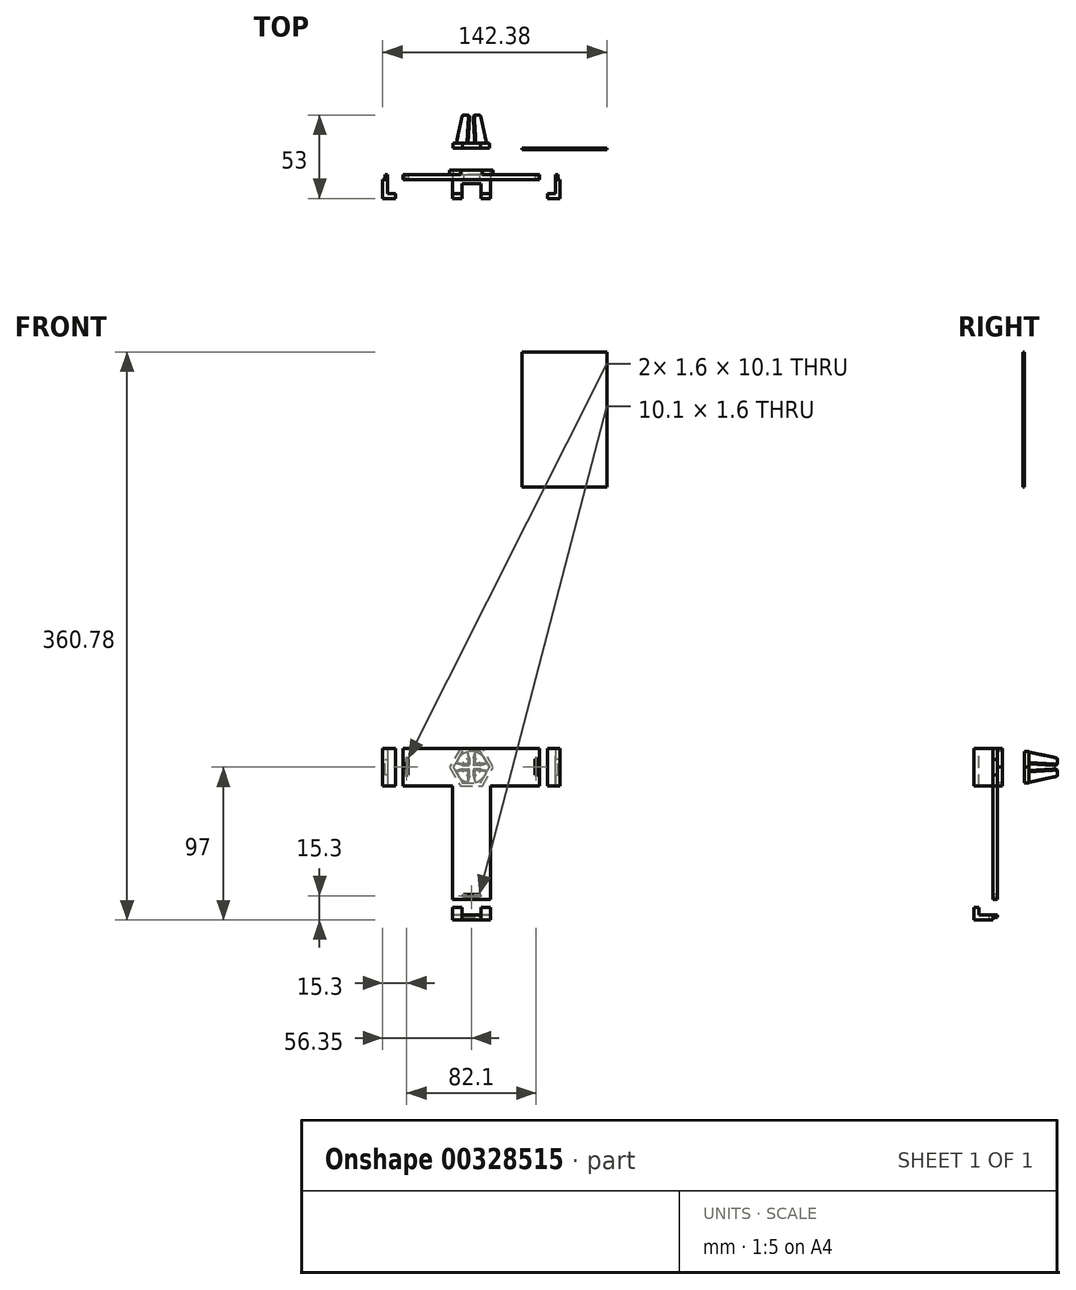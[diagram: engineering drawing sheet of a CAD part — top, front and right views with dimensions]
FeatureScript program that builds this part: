
annotation { "Feature Type Name" : "Feature", "Feature Type Description" : "" }
export const myFeature = defineFeature(function(context is Context, id is Id, definition is map)
    precondition{}
    {
        {
            assignVariable(context, id + "F0", {"name" : "depth_phone", "anyValue" : 8.5});
        }
        {
            var Q0;
            Q0=qCreatedBy(makeId("Front.planeOp"),FACE);
            var sketch = newSketch(context, id + "F1", { "sketchPlane" : qUnion([Q0])});
            skCircle(sketch, "E0", {"center": v(0, 0) * mm, "radius": 10 * mm});
            skSolve(sketch);
        }
        {
            var Q0;
            Q0=qSketchRegion(id+"F1",true);
            extrude(context, id + "F2", {"entities" : qUnion([Q0]), "oppositeDirection" : true, "depth" : 3 * mm});
        }
        {
            var Q0;
            Q0=makeQuery(id+"F2.opExtrude","CAP_FACE",FACE,{"disambiguationData":[OSD([sQuery(id+"F1.wireOp",EDGE,"E0")])],"isStart":false});
            var sketch = newSketch(context, id + "F3", { "sketchPlane" : qUnion([Q0])});
            skLineSegment(sketch, "E1.top", {"start": v(-9.75, 2.2) * mm, "end": v(-2.2, 2.2) * mm});
            skLineSegment(sketch, "E1.right", {"start": v(-2.2, 9.75) * mm, "end": v(-2.2, 2.2) * mm});
            skArc(sketch, "E2", {"start": v(-2.2, 9.75) * mm, "mid": v(-7.07, 7.07) * mm, "end": v(-9.75, 2.2) * mm});
            skLineSegment(sketch, "E3.1.0", {"start": v(-9.75, -2.2) * mm, "end": v(-2.2, -2.2) * mm});
            skLineSegment(sketch, "E3.1.1", {"start": v(-2.2, -9.75) * mm, "end": v(-2.2, -2.2) * mm});
            skArc(sketch, "E3.1.2", {"start": v(-9.75, -2.2) * mm, "mid": v(-7.07, -7.07) * mm, "end": v(-2.2, -9.75) * mm});
            skLineSegment(sketch, "E3.2.0", {"start": v(2.2, -9.75) * mm, "end": v(2.2, -2.2) * mm});
            skLineSegment(sketch, "E3.2.1", {"start": v(9.75, -2.2) * mm, "end": v(2.2, -2.2) * mm});
            skArc(sketch, "E3.2.2", {"start": v(2.2, -9.75) * mm, "mid": v(7.07, -7.07) * mm, "end": v(9.75, -2.2) * mm});
            skLineSegment(sketch, "E4.2.3.0", {"start": v(9.75, 2.2) * mm, "end": v(2.2, 2.2) * mm});
            skLineSegment(sketch, "E4.3.3.0", {"start": v(2.2, 9.75) * mm, "end": v(2.2, 2.2) * mm});
            skArc(sketch, "E4.6.3.0", {"start": v(9.75, 2.2) * mm, "mid": v(7.07, 7.07) * mm, "end": v(2.2, 9.75) * mm});
            skSolve(sketch);
        }
        {
            var Q0;
            Q0=makeQuery(id+"F3.imprint","IMPRINT",FACE,{"disambiguationData":[TD([[makeQuery(id+"F3.imprint","IMPRINT",EDGE,{"derivedFrom":sQuery(id+"F3.wireOp",EDGE,"E1.top")}),-1.0]])]});
            cPlane(context, id + "F4", {"entities" : qUnion([Q0]), "cplaneType" : CPlaneType.OFFSET, "offset" : 18 * mm, "width" : 150 * mm, "height" : 150 * mm});
        }
        {
            var Q0;
            Q0=qCreatedBy(id+"F4.planeOp",FACE);
            var sketch = newSketch(context, id + "F5", { "sketchPlane" : qUnion([Q0])});
            skLineSegment(sketch, "E5.top", {"start": v(-5.9, 1.1) * mm, "end": v(-1.1, 1.1) * mm});
            skLineSegment(sketch, "E5.right", {"start": v(-1.11, 5.9) * mm, "end": v(-1.11, 1.1) * mm});
            skArc(sketch, "E6", {"start": v(-1.11, 5.9) * mm, "mid": v(-4.24, 4.24) * mm, "end": v(-5.9, 1.1) * mm});
            skLineSegment(sketch, "E7.1.0", {"start": v(-5.9, -1.1) * mm, "end": v(-1.1, -1.1) * mm});
            skLineSegment(sketch, "E7.1.1", {"start": v(-1.1, -5.9) * mm, "end": v(-1.11, -1.1) * mm});
            skArc(sketch, "E7.1.2", {"start": v(-5.9, -1.1) * mm, "mid": v(-4.24, -4.24) * mm, "end": v(-1.1, -5.9) * mm});
            skLineSegment(sketch, "E7.2.0", {"start": v(1.1, -5.9) * mm, "end": v(1.1, -1.1) * mm});
            skLineSegment(sketch, "E7.2.1", {"start": v(5.9, -1.1) * mm, "end": v(1.1, -1.11) * mm});
            skArc(sketch, "E7.2.2", {"start": v(1.1, -5.9) * mm, "mid": v(4.24, -4.24) * mm, "end": v(5.9, -1.1) * mm});
            skLineSegment(sketch, "E7.3.0", {"start": v(5.9, 1.1) * mm, "end": v(1.1, 1.1) * mm});
            skLineSegment(sketch, "E7.3.1", {"start": v(1.1, 5.9) * mm, "end": v(1.11, 1.1) * mm});
            skArc(sketch, "E7.3.2", {"start": v(5.9, 1.11) * mm, "mid": v(4.24, 4.24) * mm, "end": v(1.1, 5.9) * mm});
            skSolve(sketch);
        }
        {
            var Q1;
            Q1=makeQuery(id+"F5.imprint","IMPRINT",FACE,{"disambiguationData":[TD([[makeQuery(id+"F5.imprint","IMPRINT",EDGE,{"derivedFrom":sQuery(id+"F5.wireOp",EDGE,"E5.top")}),1.0]])]});
            var Q2;
            Q2=makeQuery(id+"F3.imprint","IMPRINT",FACE,{"disambiguationData":[TD([[makeQuery(id+"F3.imprint","IMPRINT",EDGE,{"derivedFrom":sQuery(id+"F3.wireOp",EDGE,"E1.top")}),1.0]])]});
            loft(context, id + "F6", {"operationType" : NewBodyOperationType.ADD, "sheetProfilesArray" : [{ "sheetProfileEntities" : qUnion([Q1]) }, { "sheetProfileEntities" : qUnion([Q2]) }]});
        }
        {
            var Q1;
            Q1=makeQuery(id+"F3.imprint","IMPRINT",FACE,{"disambiguationData":[TD([[makeQuery(id+"F3.imprint","IMPRINT",EDGE,{"derivedFrom":sQuery(id+"F3.wireOp",EDGE,"E4.2.3.0")}),-1.0]])]});
            var Q2;
            Q2=makeQuery(id+"F5.imprint","IMPRINT",FACE,{"disambiguationData":[TD([[makeQuery(id+"F5.imprint","IMPRINT",EDGE,{"derivedFrom":sQuery(id+"F5.wireOp",EDGE,"E7.3.0")}),-1.0]])]});
            loft(context, id + "F7", {"operationType" : NewBodyOperationType.ADD, "sheetProfilesArray" : [{ "sheetProfileEntities" : qUnion([Q1]) }, { "sheetProfileEntities" : qUnion([Q2]) }]});
        }
        {
            var Q1;
            Q1=makeQuery(id+"F3.imprint","IMPRINT",FACE,{"disambiguationData":[TD([[makeQuery(id+"F3.imprint","IMPRINT",EDGE,{"derivedFrom":sQuery(id+"F3.wireOp",EDGE,"E3.1.0")}),-1.0]])]});
            var Q2;
            Q2=makeQuery(id+"F5.imprint","IMPRINT",FACE,{"disambiguationData":[TD([[makeQuery(id+"F5.imprint","IMPRINT",EDGE,{"derivedFrom":sQuery(id+"F5.wireOp",EDGE,"E7.1.0")}),-1.0]])]});
            loft(context, id + "F8", {"operationType" : NewBodyOperationType.ADD, "sheetProfilesArray" : [{ "sheetProfileEntities" : qUnion([Q1]) }, { "sheetProfileEntities" : qUnion([Q2]) }]});
        }
        {
            var Q1;
            Q1=makeQuery(id+"F3.imprint","IMPRINT",FACE,{"disambiguationData":[TD([[makeQuery(id+"F3.imprint","IMPRINT",EDGE,{"derivedFrom":sQuery(id+"F3.wireOp",EDGE,"E3.2.0")}),-1.0]])]});
            var Q2;
            Q2=makeQuery(id+"F5.imprint","IMPRINT",FACE,{"disambiguationData":[TD([[makeQuery(id+"F5.imprint","IMPRINT",EDGE,{"derivedFrom":sQuery(id+"F5.wireOp",EDGE,"E7.2.0")}),-1.0]])]});
            loft(context, id + "F9", {"operationType" : NewBodyOperationType.ADD, "sheetProfilesArray" : [{ "sheetProfileEntities" : qUnion([Q1]) }, { "sheetProfileEntities" : qUnion([Q2]) }]});
        }
        {
            var Q0;
            {var subQ0=sQuery(id+"F5.wireOp",EDGE,"E6");var subQ1=sQuery(id+"F5.wireOp",EDGE,"E5.right");var subQ2=sQuery(id+"F5.wireOp",EDGE,"E5.top");Q0=makeQuery(id+"F6.opLoft","MID_CAP_EDGE",EDGE,{"disambiguationData":[OSD([subQ2,subQ1,subQ0]),TDD([makeQuery(id+"F5.imprint","INTERSECT",VERTEX,{"derivedFrom":[subQ2,subQ0]}),makeQuery(id+"F5.imprint","INTERSECT",VERTEX,{"derivedFrom":[subQ1,subQ0]}),makeQuery(id+"F5.imprint","IMPRINT",EDGE,{"derivedFrom":subQ0})])],"capPos":0.0});}
            var Q1;
            Q1=makeQuery(id+"F6.opLoft","SWEPT_EDGE",EDGE,{"disambiguationData":[OSD([sQuery(id+"F3.wireOp",EDGE,"E1.right"),sQuery(id+"F3.wireOp",EDGE,"E2"),sQuery(id+"F5.wireOp",EDGE,"E5.right"),sQuery(id+"F5.wireOp",EDGE,"E6")])]});
            var Q2;
            Q2=makeQuery(id+"F6.opLoft","SWEPT_EDGE",EDGE,{"disambiguationData":[OSD([sQuery(id+"F3.wireOp",EDGE,"E1.top"),sQuery(id+"F3.wireOp",EDGE,"E1.right"),sQuery(id+"F5.wireOp",EDGE,"E5.top"),sQuery(id+"F5.wireOp",EDGE,"E5.right")])]});
            var Q3;
            Q3=makeQuery(id+"F6.opLoft","SWEPT_EDGE",EDGE,{"disambiguationData":[OSD([sQuery(id+"F3.wireOp",EDGE,"E1.top"),sQuery(id+"F3.wireOp",EDGE,"E2"),sQuery(id+"F5.wireOp",EDGE,"E5.top"),sQuery(id+"F5.wireOp",EDGE,"E6")])]});
            var Q4;
            {var subQ0=sQuery(id+"F5.wireOp",EDGE,"E7.1.2");var subQ1=sQuery(id+"F5.wireOp",EDGE,"E7.1.1");var subQ2=sQuery(id+"F5.wireOp",EDGE,"E7.1.0");Q4=makeQuery(id+"F8.opLoft","MID_CAP_EDGE",EDGE,{"disambiguationData":[OSD([subQ2,subQ1,subQ0]),TDD([makeQuery(id+"F5.imprint","INTERSECT",VERTEX,{"derivedFrom":[subQ2,subQ0]}),makeQuery(id+"F5.imprint","INTERSECT",VERTEX,{"derivedFrom":[subQ1,subQ0]}),makeQuery(id+"F5.imprint","IMPRINT",EDGE,{"derivedFrom":subQ0})])],"capPos":1.0});}
            var Q5;
            Q5=makeQuery(id+"F8.opLoft","SWEPT_EDGE",EDGE,{"disambiguationData":[OSD([sQuery(id+"F3.wireOp",EDGE,"E3.1.0"),sQuery(id+"F3.wireOp",EDGE,"E3.1.2"),sQuery(id+"F5.wireOp",EDGE,"E7.1.0"),sQuery(id+"F5.wireOp",EDGE,"E7.1.2")])]});
            var Q6;
            Q6=makeQuery(id+"F8.opLoft","SWEPT_EDGE",EDGE,{"disambiguationData":[OSD([sQuery(id+"F3.wireOp",EDGE,"E3.1.0"),sQuery(id+"F3.wireOp",EDGE,"E3.1.1"),sQuery(id+"F5.wireOp",EDGE,"E7.1.0"),sQuery(id+"F5.wireOp",EDGE,"E7.1.1")])]});
            var Q7;
            Q7=makeQuery(id+"F8.opLoft","SWEPT_EDGE",EDGE,{"disambiguationData":[OSD([sQuery(id+"F3.wireOp",EDGE,"E3.1.1"),sQuery(id+"F3.wireOp",EDGE,"E3.1.2"),sQuery(id+"F5.wireOp",EDGE,"E7.1.1"),sQuery(id+"F5.wireOp",EDGE,"E7.1.2")])]});
            var Q8;
            {var subQ0=sQuery(id+"F5.wireOp",EDGE,"E7.2.2");var subQ1=sQuery(id+"F5.wireOp",EDGE,"E7.2.1");var subQ2=sQuery(id+"F5.wireOp",EDGE,"E7.2.0");Q8=makeQuery(id+"F9.opLoft","MID_CAP_EDGE",EDGE,{"disambiguationData":[OSD([subQ2,subQ1,subQ0]),TDD([makeQuery(id+"F5.imprint","INTERSECT",VERTEX,{"derivedFrom":[subQ2,subQ0]}),makeQuery(id+"F5.imprint","INTERSECT",VERTEX,{"derivedFrom":[subQ1,subQ0]}),makeQuery(id+"F5.imprint","IMPRINT",EDGE,{"derivedFrom":subQ0})])],"capPos":1.0});}
            var Q9;
            Q9=makeQuery(id+"F9.opLoft","SWEPT_EDGE",EDGE,{"disambiguationData":[OSD([sQuery(id+"F3.wireOp",EDGE,"E3.2.0"),sQuery(id+"F3.wireOp",EDGE,"E3.2.2"),sQuery(id+"F5.wireOp",EDGE,"E7.2.0"),sQuery(id+"F5.wireOp",EDGE,"E7.2.2")])]});
            var Q10;
            Q10=makeQuery(id+"F9.opLoft","SWEPT_EDGE",EDGE,{"disambiguationData":[OSD([sQuery(id+"F3.wireOp",EDGE,"E3.2.1"),sQuery(id+"F3.wireOp",EDGE,"E3.2.2"),sQuery(id+"F5.wireOp",EDGE,"E7.2.1"),sQuery(id+"F5.wireOp",EDGE,"E7.2.2")])]});
            var Q11;
            Q11=makeQuery(id+"F9.opLoft","SWEPT_EDGE",EDGE,{"disambiguationData":[OSD([sQuery(id+"F3.wireOp",EDGE,"E3.2.0"),sQuery(id+"F3.wireOp",EDGE,"E3.2.1"),sQuery(id+"F5.wireOp",EDGE,"E7.2.0"),sQuery(id+"F5.wireOp",EDGE,"E7.2.1")])]});
            var Q12;
            {var subQ0=sQuery(id+"F5.wireOp",EDGE,"E7.3.2");var subQ1=sQuery(id+"F5.wireOp",EDGE,"E7.3.1");var subQ2=sQuery(id+"F5.wireOp",EDGE,"E7.3.0");Q12=makeQuery(id+"F7.opLoft","MID_CAP_EDGE",EDGE,{"disambiguationData":[OSD([subQ2,subQ1,subQ0]),TDD([makeQuery(id+"F5.imprint","INTERSECT",VERTEX,{"derivedFrom":[subQ2,subQ0]}),makeQuery(id+"F5.imprint","INTERSECT",VERTEX,{"derivedFrom":[subQ1,subQ0]}),makeQuery(id+"F5.imprint","IMPRINT",EDGE,{"derivedFrom":subQ0})])],"capPos":1.0});}
            var Q13;
            Q13=makeQuery(id+"F7.opLoft","SWEPT_EDGE",EDGE,{"disambiguationData":[OSD([sQuery(id+"F3.wireOp",EDGE,"E4.2.3.0"),sQuery(id+"F3.wireOp",EDGE,"E4.3.3.0"),sQuery(id+"F5.wireOp",EDGE,"E7.3.0"),sQuery(id+"F5.wireOp",EDGE,"E7.3.1")])]});
            var Q14;
            Q14=makeQuery(id+"F7.opLoft","SWEPT_EDGE",EDGE,{"disambiguationData":[OSD([sQuery(id+"F3.wireOp",EDGE,"E4.2.3.0"),sQuery(id+"F3.wireOp",EDGE,"E4.6.3.0"),sQuery(id+"F5.wireOp",EDGE,"E7.3.0"),sQuery(id+"F5.wireOp",EDGE,"E7.3.2")])]});
            var Q15;
            Q15=makeQuery(id+"F7.opLoft","SWEPT_EDGE",EDGE,{"disambiguationData":[OSD([sQuery(id+"F3.wireOp",EDGE,"E4.3.3.0"),sQuery(id+"F3.wireOp",EDGE,"E4.6.3.0"),sQuery(id+"F5.wireOp",EDGE,"E7.3.1"),sQuery(id+"F5.wireOp",EDGE,"E7.3.2")])]});
            fillet(context, id + "F10", {"entities" : qUnion([Q0, Q1, Q2, Q3, Q4, Q5, Q6, Q7, Q8, Q9, Q10, Q11, Q12, Q13, Q14, Q15]), "radius" : .5 * mm, "tangentPropagation" : true, "allowEdgeOverflow" : false});
        }
        {
            var Q0;
            Q0=qCreatedBy(makeId("Front.planeOp"),FACE);
            var sketch = newSketch(context, id + "F11", { "sketchPlane" : qUnion([Q0])});
            skLineSegment(sketch, "E8.bottom", {"start": v(86.03, 177.78) * mm, "end": v(32.03, 177.78) * mm});
            skLineSegment(sketch, "E8.top", {"start": v(86.03, 263.78) * mm, "end": v(32.03, 263.78) * mm});
            skLineSegment(sketch, "E8.left", {"start": v(86.03, 177.78) * mm, "end": v(86.03, 263.78) * mm});
            skLineSegment(sketch, "E8.right", {"start": v(32.03, 177.78) * mm, "end": v(32.03, 263.78) * mm});
            skSolve(sketch);
        }
        {
            var Q0;
            Q0=makeQuery(id+"F11.imprint","IMPRINT",FACE,{"disambiguationData":[TD([[makeQuery(id+"F11.imprint","IMPRINT",EDGE,{"derivedFrom":sQuery(id+"F11.wireOp",EDGE,"E8.bottom")}),-1.0]])]});
            extrude(context, id + "F12", {"entities" : qUnion([Q0]), "depth" : 1 * mm});
        }
        {
            var Q0;
            {var subQ0=sQuery(id+"F5.wireOp",EDGE,"E5.right");var subQ1=sQuery(id+"F5.wireOp",EDGE,"E6");var subQ2=sQuery(id+"F5.wireOp",EDGE,"E5.top");Q0=makeQuery(id+"F6.opLoft","MID_CAP_EDGE",EDGE,{"disambiguationData":[OSD([subQ2,subQ0,subQ1]),TDD([makeQuery(id+"F5.imprint","INTERSECT",VERTEX,{"derivedFrom":[subQ2,subQ0]}),makeQuery(id+"F5.imprint","INTERSECT",VERTEX,{"derivedFrom":[subQ0,subQ1]}),makeQuery(id+"F5.imprint","IMPRINT",EDGE,{"derivedFrom":subQ0})])],"capPos":0.0});}
            var Q1;
            {var subQ0=sQuery(id+"F5.wireOp",EDGE,"E5.top");var subQ1=sQuery(id+"F5.wireOp",EDGE,"E5.right");var subQ2=sQuery(id+"F5.wireOp",EDGE,"E6");Q1=makeQuery(id+"F6.opLoft","MID_CAP_EDGE",EDGE,{"disambiguationData":[OSD([subQ0,subQ1,subQ2]),TDD([makeQuery(id+"F5.imprint","INTERSECT",VERTEX,{"derivedFrom":[subQ0,subQ2]}),makeQuery(id+"F5.imprint","INTERSECT",VERTEX,{"derivedFrom":[subQ0,subQ1]}),makeQuery(id+"F5.imprint","IMPRINT",EDGE,{"derivedFrom":subQ0})])],"capPos":0.0});}
            var Q2;
            {var subQ0=sQuery(id+"F5.wireOp",EDGE,"E7.1.0");var subQ1=sQuery(id+"F5.wireOp",EDGE,"E7.1.1");var subQ2=sQuery(id+"F5.wireOp",EDGE,"E7.1.2");Q2=makeQuery(id+"F8.opLoft","MID_CAP_EDGE",EDGE,{"disambiguationData":[OSD([subQ0,subQ1,subQ2]),TDD([makeQuery(id+"F5.imprint","INTERSECT",VERTEX,{"derivedFrom":[subQ0,subQ2]}),makeQuery(id+"F5.imprint","INTERSECT",VERTEX,{"derivedFrom":[subQ0,subQ1]}),makeQuery(id+"F5.imprint","IMPRINT",EDGE,{"derivedFrom":subQ0})])],"capPos":1.0});}
            var Q3;
            {var subQ0=sQuery(id+"F5.wireOp",EDGE,"E7.1.1");var subQ1=sQuery(id+"F5.wireOp",EDGE,"E7.1.2");var subQ2=sQuery(id+"F5.wireOp",EDGE,"E7.1.0");Q3=makeQuery(id+"F8.opLoft","MID_CAP_EDGE",EDGE,{"disambiguationData":[OSD([subQ2,subQ0,subQ1]),TDD([makeQuery(id+"F5.imprint","INTERSECT",VERTEX,{"derivedFrom":[subQ2,subQ0]}),makeQuery(id+"F5.imprint","INTERSECT",VERTEX,{"derivedFrom":[subQ0,subQ1]}),makeQuery(id+"F5.imprint","IMPRINT",EDGE,{"derivedFrom":subQ0})])],"capPos":1.0});}
            var Q4;
            {var subQ0=sQuery(id+"F5.wireOp",EDGE,"E7.2.0");var subQ1=sQuery(id+"F5.wireOp",EDGE,"E7.2.1");var subQ2=sQuery(id+"F5.wireOp",EDGE,"E7.2.2");Q4=makeQuery(id+"F9.opLoft","MID_CAP_EDGE",EDGE,{"disambiguationData":[OSD([subQ0,subQ1,subQ2]),TDD([makeQuery(id+"F5.imprint","INTERSECT",VERTEX,{"derivedFrom":[subQ0,subQ2]}),makeQuery(id+"F5.imprint","INTERSECT",VERTEX,{"derivedFrom":[subQ0,subQ1]}),makeQuery(id+"F5.imprint","IMPRINT",EDGE,{"derivedFrom":subQ0})])],"capPos":1.0});}
            var Q5;
            {var subQ0=sQuery(id+"F5.wireOp",EDGE,"E7.2.1");var subQ1=sQuery(id+"F5.wireOp",EDGE,"E7.2.2");var subQ2=sQuery(id+"F5.wireOp",EDGE,"E7.2.0");Q5=makeQuery(id+"F9.opLoft","MID_CAP_EDGE",EDGE,{"disambiguationData":[OSD([subQ2,subQ0,subQ1]),TDD([makeQuery(id+"F5.imprint","INTERSECT",VERTEX,{"derivedFrom":[subQ2,subQ0]}),makeQuery(id+"F5.imprint","INTERSECT",VERTEX,{"derivedFrom":[subQ0,subQ1]}),makeQuery(id+"F5.imprint","IMPRINT",EDGE,{"derivedFrom":subQ0})])],"capPos":1.0});}
            var Q6;
            {var subQ0=sQuery(id+"F5.wireOp",EDGE,"E7.3.0");var subQ1=sQuery(id+"F5.wireOp",EDGE,"E7.3.1");var subQ2=sQuery(id+"F5.wireOp",EDGE,"E7.3.2");Q6=makeQuery(id+"F7.opLoft","MID_CAP_EDGE",EDGE,{"disambiguationData":[OSD([subQ0,subQ1,subQ2]),TDD([makeQuery(id+"F5.imprint","INTERSECT",VERTEX,{"derivedFrom":[subQ0,subQ2]}),makeQuery(id+"F5.imprint","INTERSECT",VERTEX,{"derivedFrom":[subQ0,subQ1]}),makeQuery(id+"F5.imprint","IMPRINT",EDGE,{"derivedFrom":subQ0})])],"capPos":1.0});}
            var Q7;
            {var subQ0=sQuery(id+"F5.wireOp",EDGE,"E7.3.1");var subQ1=sQuery(id+"F5.wireOp",EDGE,"E7.3.2");var subQ2=sQuery(id+"F5.wireOp",EDGE,"E7.3.0");Q7=makeQuery(id+"F7.opLoft","MID_CAP_EDGE",EDGE,{"disambiguationData":[OSD([subQ2,subQ0,subQ1]),TDD([makeQuery(id+"F5.imprint","INTERSECT",VERTEX,{"derivedFrom":[subQ2,subQ0]}),makeQuery(id+"F5.imprint","INTERSECT",VERTEX,{"derivedFrom":[subQ0,subQ1]}),makeQuery(id+"F5.imprint","IMPRINT",EDGE,{"derivedFrom":subQ0})])],"capPos":1.0});}
            fillet(context, id + "F13", {"entities" : qUnion([Q0, Q1, Q2, Q3, Q4, Q5, Q6, Q7]), "radius" : 1.5 * mm, "tangentPropagation" : true, "allowEdgeOverflow" : false});
        }
        {
            var Q0;
            Q0=qCreatedBy(makeId("Front.planeOp"),FACE);
            var sketch = newSketch(context, id + "F14", { "sketchPlane" : qUnion([Q0])});
            skLineSegment(sketch, "E9.bottom", {"start": v(102.82, 54.15) * mm, "end": v(182.82, 54.15) * mm});
            skLineSegment(sketch, "E9.top", {"start": v(102.82, -107.85) * mm, "end": v(182.82, -107.85) * mm});
            skLineSegment(sketch, "E9.left", {"start": v(102.82, 54.15) * mm, "end": v(102.82, -107.85) * mm});
            skLineSegment(sketch, "E9.right", {"start": v(182.82, 54.15) * mm, "end": v(182.82, -107.85) * mm});
            skSolve(sketch);
        }
        {
            var Q0;
            Q0=qSketchRegion(id+"F14",true);
            extrude(context, id + "F15", {"entities" : qUnion([Q0]), "depth" : (getVariable(context, 'depth_phone')) * mm});
        }
        {
            var Q0;
            Q0=makeQuery(id+"F15.opExtrude","SWEPT_EDGE",EDGE,{"disambiguationData":[OSD([sQuery(id+"F14.wireOp",EDGE,"E9.bottom"),sQuery(id+"F14.wireOp",EDGE,"E9.left")])]});
            var Q1;
            Q1=makeQuery(id+"F15.opExtrude","SWEPT_EDGE",EDGE,{"disambiguationData":[OSD([sQuery(id+"F14.wireOp",EDGE,"E9.bottom"),sQuery(id+"F14.wireOp",EDGE,"E9.right")])]});
            var Q2;
            Q2=makeQuery(id+"F15.opExtrude","SWEPT_EDGE",EDGE,{"disambiguationData":[OSD([sQuery(id+"F14.wireOp",EDGE,"E9.top"),sQuery(id+"F14.wireOp",EDGE,"E9.right")])]});
            var Q3;
            Q3=makeQuery(id+"F15.opExtrude","SWEPT_EDGE",EDGE,{"disambiguationData":[OSD([sQuery(id+"F14.wireOp",EDGE,"E9.top"),sQuery(id+"F14.wireOp",EDGE,"E9.left")])]});
            fillet(context, id + "F16", {"entities" : qUnion([Q0, Q1, Q2, Q3]), "radius" : 2.5 * mm, "tangentPropagation" : true, "allowEdgeOverflow" : false});
        }
        {
            var Q0;
            Q0=makeQuery(id+"F15.opExtrude","CAP_EDGE",EDGE,{"disambiguationData":[OSD([sQuery(id+"F14.wireOp",EDGE,"E9.right")])],"isStart":true});
            var Q1;
            Q1=makeQuery(id+"F15.opExtrude","CAP_EDGE",EDGE,{"disambiguationData":[OSD([sQuery(id+"F14.wireOp",EDGE,"E9.bottom")])],"isStart":true});
            var Q2;
            Q2=makeQuery(id+"F15.opExtrude","CAP_EDGE",EDGE,{"disambiguationData":[OSD([sQuery(id+"F14.wireOp",EDGE,"E9.left")])],"isStart":true});
            var Q3;
            Q3=makeQuery(id+"F15.opExtrude","CAP_EDGE",EDGE,{"disambiguationData":[OSD([sQuery(id+"F14.wireOp",EDGE,"E9.top")])],"isStart":true});
            fillet(context, id + "F17", {"entities" : qUnion([Q0, Q1, Q2, Q3]), "radius" : 2.5 * mm, "tangentPropagation" : true, "allowEdgeOverflow" : false});
        }
        {
            var Q0;
            Q0=makeQuery(id+"F15.opExtrude","CAP_EDGE",EDGE,{"disambiguationData":[OSD([sQuery(id+"F14.wireOp",EDGE,"E9.right")])],"isStart":false});
            var Q1;
            Q1=makeQuery(id+"F15.opExtrude","CAP_EDGE",EDGE,{"disambiguationData":[OSD([sQuery(id+"F14.wireOp",EDGE,"E9.bottom")])],"isStart":false});
            var Q2;
            Q2=makeQuery(id+"F15.opExtrude","CAP_EDGE",EDGE,{"disambiguationData":[OSD([sQuery(id+"F14.wireOp",EDGE,"E9.left")])],"isStart":false});
            var Q3;
            Q3=makeQuery(id+"F15.opExtrude","CAP_EDGE",EDGE,{"disambiguationData":[OSD([sQuery(id+"F14.wireOp",EDGE,"E9.top")])],"isStart":false});
            fillet(context, id + "F18", {"entities" : qUnion([Q0, Q1, Q2, Q3]), "radius" : 12 * mm, "tangentPropagation" : true, "allowEdgeOverflow" : false});
        }
        {
            var Q0;
            Q0=qCreatedBy(makeId("Front.planeOp"),FACE);
            cPlane(context, id + "F19", {"entities" : qUnion([Q0]), "cplaneType" : CPlaneType.OFFSET, "offset" : 20 * mm, "width" : 150 * mm, "height" : 150 * mm});
        }
        {
            var Q0;
            Q0=qCreatedBy(id+"F19.planeOp",FACE);
            var sketch = newSketch(context, id + "F20", { "sketchPlane" : qUnion([Q0])});
            skLineSegment(sketch, "E10.bottom", {"start": v(-12, -84) * mm, "end": v(12, -84) * mm});
            skLineSegment(sketch, "E10.top", {"start": v(-12, 0) * mm, "end": v(12, 0) * mm});
            skLineSegment(sketch, "E10.left", {"start": v(-12, -84) * mm, "end": v(-12, 0) * mm});
            skLineSegment(sketch, "E10.right", {"start": v(12, -84) * mm, "end": v(12, 0) * mm});
            skSolve(sketch);
        }
        {
            var Q0;
            Q0=qSketchRegion(id+"F20",true);
            extrude(context, id + "F21", {"entities" : qUnion([Q0]), "operationType" : NewBodyOperationType.ADD, "oppositeDirection" : true, "depth" : 3 * mm});
        }
        {
            var Q0;
            Q0=makeQuery(id+"F21.opExtrude","SWEPT_FACE",FACE,{"disambiguationData":[OSD([sQuery(id+"F20.wireOp",EDGE,"E10.bottom")])]});
            cPlane(context, id + "F22", {"entities" : qUnion([Q0]), "cplaneType" : CPlaneType.OFFSET, "offset" : 10 * mm, "width" : 150 * mm, "height" : 150 * mm});
        }
        {
            var Q0;
            Q0=qCreatedBy(id+"F22.planeOp",FACE);
            var sketch = newSketch(context, id + "F23", { "sketchPlane" : qUnion([Q0])});
            skLineSegment(sketch, "E11.bottom", {"start": v(12, 17) * mm, "end": v(-12, 17) * mm});
            skLineSegment(sketch, "E11.top", {"start": v(12, 29) * mm, "end": v(-12, 29) * mm});
            skLineSegment(sketch, "E11.left", {"start": v(12, 17) * mm, "end": v(12, 29) * mm});
            skLineSegment(sketch, "E11.right", {"start": v(-12, 17) * mm, "end": v(-12, 29) * mm});
            skSolve(sketch);
        }
        {
            var Q0;
            Q0=qSketchRegion(id+"F23",true);
            extrude(context, id + "F24", {"entities" : qUnion([Q0]), "operationType" : NewBodyOperationType.ADD, "depth" : 3 * mm});
        }
        {
            var Q0;
            Q0=qCreatedBy(id+"F19.planeOp",FACE);
            var sketch = newSketch(context, id + "F25", { "sketchPlane" : qUnion([Q0])});
            skLineSegment(sketch, "E12.bottom", {"start": v(43.35, 12) * mm, "end": v(-43.35, 12) * mm});
            skLineSegment(sketch, "E12.top", {"start": v(43.35, -12) * mm, "end": v(-43.35, -12) * mm});
            skLineSegment(sketch, "E12.left", {"start": v(43.35, 12) * mm, "end": v(43.35, -12) * mm});
            skLineSegment(sketch, "E12.right", {"start": v(-43.35, 12) * mm, "end": v(-43.35, -12) * mm});
            skLineSegment(sketch, "E13", {"start": v(43.35, 0) * mm, "end": v(-43.35, 0) * mm, "construction": true});
            skLineSegment(sketch, "E14", {"start": v(0, -12) * mm, "end": v(0, 12) * mm, "construction": true});
            skPoint(sketch, "E15", {"position": v(0, 0) * mm});
            skSolve(sketch);
        }
        {
            var Q0;
            Q0=makeQuery(id+"F25.imprint","IMPRINT",FACE,{"disambiguationData":[TD([[makeQuery(id+"F25.imprint","IMPRINT",EDGE,{"derivedFrom":sQuery(id+"F25.wireOp",EDGE,"E12.bottom")}),1.0]])]});
            extrude(context, id + "F26", {"entities" : qUnion([Q0]), "operationType" : NewBodyOperationType.ADD, "oppositeDirection" : true, "depth" : 3 * mm});
        }
        {
            var Q0;
            Q0=makeQuery(id+"F26.opExtrude","SWEPT_FACE",FACE,{"disambiguationData":[OSD([sQuery(id+"F25.wireOp",EDGE,"E12.right")])]});
            cPlane(context, id + "F27", {"entities" : qUnion([Q0]), "cplaneType" : CPlaneType.OFFSET, "offset" : 10 * mm, "width" : 150 * mm, "height" : 150 * mm});
        }
        {
            var Q0;
            Q0=qCreatedBy(id+"F27.planeOp",FACE);
            var sketch = newSketch(context, id + "F28", { "sketchPlane" : qUnion([Q0])});
            skLineSegment(sketch, "E16.bottom", {"start": v(17, 12) * mm, "end": v(29, 12) * mm});
            skLineSegment(sketch, "E16.top", {"start": v(17, -12) * mm, "end": v(29, -12) * mm});
            skLineSegment(sketch, "E16.left", {"start": v(17, 12) * mm, "end": v(17, -12) * mm});
            skLineSegment(sketch, "E16.right", {"start": v(29, 12) * mm, "end": v(29, -12) * mm});
            skSolve(sketch);
        }
        {
            var Q0;
            Q0=qSketchRegion(id+"F28",true);
            extrude(context, id + "F29", {"entities" : qUnion([Q0]), "operationType" : NewBodyOperationType.ADD, "depth" : 3 * mm});
        }
        {
            var Q0;
            Q0=makeQuery(id+"F26.opExtrude","SWEPT_FACE",FACE,{"disambiguationData":[OSD([sQuery(id+"F25.wireOp",EDGE,"E12.left")])]});
            cPlane(context, id + "F30", {"entities" : qUnion([Q0]), "cplaneType" : CPlaneType.OFFSET, "offset" : 10 * mm, "width" : 150 * mm, "height" : 150 * mm});
        }
        {
            var Q0;
            Q0=qCreatedBy(id+"F30.planeOp",FACE);
            var sketch = newSketch(context, id + "F31", { "sketchPlane" : qUnion([Q0])});
            skLineSegment(sketch, "E17.bottom", {"start": v(-17, -12) * mm, "end": v(-29, -12) * mm});
            skLineSegment(sketch, "E17.top", {"start": v(-17, 12) * mm, "end": v(-29, 12) * mm});
            skLineSegment(sketch, "E17.left", {"start": v(-17, -12) * mm, "end": v(-17, 12) * mm});
            skLineSegment(sketch, "E17.right", {"start": v(-29, -12) * mm, "end": v(-29, 12) * mm});
            skSolve(sketch);
        }
        {
            var Q0;
            Q0=qSketchRegion(id+"F31",true);
            extrude(context, id + "F32", {"entities" : qUnion([Q0]), "operationType" : NewBodyOperationType.ADD, "depth" : 3 * mm});
        }
        {
            var Q0;
            Q0=makeQuery(id+"F24.opExtrude","CAP_FACE",FACE,{"disambiguationData":[OSD([sQuery(id+"F23.wireOp",EDGE,"E11.bottom"),sQuery(id+"F23.wireOp",EDGE,"E11.top"),sQuery(id+"F23.wireOp",EDGE,"E11.left"),sQuery(id+"F23.wireOp",EDGE,"E11.right")])],"isStart":false});
            var sketch = newSketch(context, id + "F33", { "sketchPlane" : qUnion([Q0])});
            skLineSegment(sketch, "E18.bottom", {"start": v(-6, 29) * mm, "end": v(6, 29) * mm});
            skLineSegment(sketch, "E18.top", {"start": v(-6, 20) * mm, "end": v(6, 20) * mm});
            skLineSegment(sketch, "E18.left", {"start": v(-6, 29) * mm, "end": v(-6, 20) * mm});
            skLineSegment(sketch, "E18.right", {"start": v(6, 29) * mm, "end": v(6, 20) * mm});
            skLineSegment(sketch, "E19", {"start": v(0, 20) * mm, "end": v(0, 29) * mm, "construction": true});
            skSolve(sketch);
        }
        {
            var Q0;
            Q0=qSketchRegion(id+"F33",true);
            extrude(context, id + "F34", {"entities" : qUnion([Q0]), "operationType" : NewBodyOperationType.REMOVE, "endBound" : BoundingType.UP_TO_NEXT, "oppositeDirection" : true, "depth" : 25 * mm});
        }
        {
            var Q0;
            Q0=makeQuery(id+"F29.opExtrude","SWEPT_FACE",FACE,{"disambiguationData":[OSD([sQuery(id+"F28.wireOp",EDGE,"E16.right")])]});
            var sketch = newSketch(context, id + "F35", { "sketchPlane" : qUnion([Q0])});
            skLineSegment(sketch, "E20.bottom", {"start": v(-56.35, -12) * mm, "end": v(-48.35, -12) * mm});
            skLineSegment(sketch, "E20.top", {"start": v(-56.35, 12) * mm, "end": v(-48.35, 12) * mm});
            skLineSegment(sketch, "E20.left", {"start": v(-56.35, -12) * mm, "end": v(-56.35, 12) * mm});
            skLineSegment(sketch, "E20.right", {"start": v(-48.35, -12) * mm, "end": v(-48.35, 12) * mm});
            skLineSegment(sketch, "E21.bottom", {"start": v(56.35, -12) * mm, "end": v(48.35, -12) * mm});
            skLineSegment(sketch, "E21.top", {"start": v(56.35, 12) * mm, "end": v(48.35, 12) * mm});
            skLineSegment(sketch, "E21.left", {"start": v(56.35, -12) * mm, "end": v(56.35, 12) * mm});
            skLineSegment(sketch, "E21.right", {"start": v(48.35, -12) * mm, "end": v(48.35, 12) * mm});
            skLineSegment(sketch, "E22.bottom", {"start": v(-12, -97) * mm, "end": v(-6, -97) * mm});
            skLineSegment(sketch, "E22.top", {"start": v(-12, -89) * mm, "end": v(-6, -89) * mm});
            skLineSegment(sketch, "E22.left", {"start": v(-12, -97) * mm, "end": v(-12, -89) * mm});
            skLineSegment(sketch, "E22.right", {"start": v(-6, -97) * mm, "end": v(-6, -89) * mm});
            skLineSegment(sketch, "E23.bottom", {"start": v(6, -97) * mm, "end": v(12, -97) * mm});
            skLineSegment(sketch, "E23.top", {"start": v(6, -89) * mm, "end": v(12, -89) * mm});
            skLineSegment(sketch, "E23.left", {"start": v(6, -97) * mm, "end": v(6, -89) * mm});
            skLineSegment(sketch, "E23.right", {"start": v(12, -97) * mm, "end": v(12, -89) * mm});
            skSolve(sketch);
        }
        {
            var Q0;
            Q0=qSketchRegion(id+"F35",true);
            extrude(context, id + "F36", {"entities" : qUnion([Q0]), "operationType" : NewBodyOperationType.ADD, "depth" : 3 * mm});
        }
        {
            var Q0;
            Q0=makeQuery(id+"F32.boolean.opBoolean","MERGE",FACE,{"derivedFrom":[makeQuery(id+"F29.boolean.opBoolean","MERGE",FACE,{"derivedFrom":[makeQuery(id+"F26.boolean.opBoolean","MERGE",FACE,{"derivedFrom":[makeQuery(id+"F24.boolean.opBoolean","MERGE",FACE,{"derivedFrom":[makeQuery(id+"F21.opExtrude","CAP_FACE",FACE,{"disambiguationData":[OSD([sQuery(id+"F20.wireOp",EDGE,"E10.bottom"),sQuery(id+"F20.wireOp",EDGE,"E10.top"),sQuery(id+"F20.wireOp",EDGE,"E10.left"),sQuery(id+"F20.wireOp",EDGE,"E10.right")])],"isStart":false}),makeQuery(id+"F24.opExtrude","SWEPT_FACE",FACE,{"disambiguationData":[OSD([sQuery(id+"F23.wireOp",EDGE,"E11.bottom")])]})]}),makeQuery(id+"F26.opExtrude","CAP_FACE",FACE,{"disambiguationData":[OSD([sQuery(id+"F25.wireOp",EDGE,"E12.bottom"),sQuery(id+"F25.wireOp",EDGE,"E12.top"),sQuery(id+"F25.wireOp",EDGE,"E12.left"),sQuery(id+"F25.wireOp",EDGE,"E12.right")])],"isStart":false})]}),makeQuery(id+"F29.opExtrude","SWEPT_FACE",FACE,{"disambiguationData":[OSD([sQuery(id+"F28.wireOp",EDGE,"E16.left")])]})]}),makeQuery(id+"F32.opExtrude","SWEPT_FACE",FACE,{"disambiguationData":[OSD([sQuery(id+"F31.wireOp",EDGE,"E17.left")])]})]});
            var sketch = newSketch(context, id + "F37", { "sketchPlane" : qUnion([Q0])});
            skCircle(sketch, "E24.cCircle", {"center": v(0, 0) * mm, "radius": 10.1 * mm, "construction": true});
            skLineSegment(sketch, "E24.0", {"start": v(11.66, 0) * mm, "end": v(5.83, -10.1) * mm});
            skLineSegment(sketch, "E24.1", {"start": v(5.83, -10.1) * mm, "end": v(-5.83, -10.1) * mm});
            skLineSegment(sketch, "E24.2", {"start": v(-5.83, -10.1) * mm, "end": v(-11.66, 0) * mm});
            skLineSegment(sketch, "E24.3", {"start": v(-11.66, 0) * mm, "end": v(-5.83, 10.1) * mm});
            skLineSegment(sketch, "E24.4", {"start": v(-5.83, 10.1) * mm, "end": v(5.83, 10.1) * mm});
            skLineSegment(sketch, "E24.5", {"start": v(5.83, 10.1) * mm, "end": v(11.66, 0) * mm});
            skPoint(sketch, "E24.0.midPoint", {"position": v(8.75, -5.05) * mm});
            skCircle(sketch, "E25.cCircle", {"center": v(0, 0) * mm, "radius": 12 * mm, "construction": true});
            skLineSegment(sketch, "E25.0", {"start": v(13.86, 0) * mm, "end": v(6.93, -12) * mm});
            skLineSegment(sketch, "E25.1", {"start": v(6.93, -12) * mm, "end": v(-6.93, -12) * mm});
            skLineSegment(sketch, "E25.2", {"start": v(-6.93, -12) * mm, "end": v(-13.86, 0) * mm});
            skLineSegment(sketch, "E25.3", {"start": v(-13.86, 0) * mm, "end": v(-6.93, 12) * mm});
            skLineSegment(sketch, "E25.4", {"start": v(-6.93, 12) * mm, "end": v(6.93, 12) * mm});
            skLineSegment(sketch, "E25.5", {"start": v(6.93, 12) * mm, "end": v(13.86, 0) * mm});
            skPoint(sketch, "E25.0.midPoint", {"position": v(10.4, -6) * mm});
            skSolve(sketch);
        }
        {
            var Q0;
            Q0=qSketchRegion(id+"F37",true);
            extrude(context, id + "F38", {"entities" : qUnion([Q0]), "operationType" : NewBodyOperationType.ADD, "depth" : 3 * mm});
        }
        {
            var Q0;
            Q0=makeQuery(id+"F2.opExtrude","CAP_FACE",FACE,{"disambiguationData":[OSD([sQuery(id+"F1.wireOp",EDGE,"E0")])],"isStart":false});
            var sketch = newSketch(context, id + "F39", { "sketchPlane" : qUnion([Q0])});
            skCircle(sketch, "E26.cCircle", {"center": v(0, 0) * mm, "radius": 10 * mm, "construction": true});
            skLineSegment(sketch, "E26.0", {"start": v(11.55, 0) * mm, "end": v(5.77, -10) * mm});
            skLineSegment(sketch, "E26.1", {"start": v(5.77, -10) * mm, "end": v(-5.77, -10) * mm});
            skLineSegment(sketch, "E26.2", {"start": v(-5.77, -10) * mm, "end": v(-11.55, 0) * mm});
            skLineSegment(sketch, "E26.3", {"start": v(-11.55, 0) * mm, "end": v(-5.77, 10) * mm});
            skLineSegment(sketch, "E26.4", {"start": v(-5.77, 10) * mm, "end": v(5.77, 10) * mm});
            skLineSegment(sketch, "E26.5", {"start": v(5.77, 10) * mm, "end": v(11.55, 0) * mm});
            skPoint(sketch, "E26.0.midPoint", {"position": v(8.66, -5) * mm});
            skSolve(sketch);
        }
        {
            var Q0;
            Q0=qSketchRegion(id+"F39",true);
            extrude(context, id + "F40", {"entities" : qUnion([Q0]), "operationType" : NewBodyOperationType.ADD, "oppositeDirection" : true, "depth" : 3 * mm});
        }
        {
            var Q0;
            Q0=makeQuery(id+"F26.boolean.opBoolean","MERGE",FACE,{"derivedFrom":[makeQuery(id+"F21.opExtrude","CAP_FACE",FACE,{"disambiguationData":[OSD([sQuery(id+"F20.wireOp",EDGE,"E10.bottom"),sQuery(id+"F20.wireOp",EDGE,"E10.top"),sQuery(id+"F20.wireOp",EDGE,"E10.left"),sQuery(id+"F20.wireOp",EDGE,"E10.right")])],"isStart":true}),makeQuery(id+"F26.opExtrude","CAP_FACE",FACE,{"disambiguationData":[OSD([sQuery(id+"F25.wireOp",EDGE,"E12.bottom"),sQuery(id+"F25.wireOp",EDGE,"E12.top"),sQuery(id+"F25.wireOp",EDGE,"E12.left"),sQuery(id+"F25.wireOp",EDGE,"E12.right")])],"isStart":true})]});
            var sketch = newSketch(context, id + "F41", { "sketchPlane" : qUnion([Q0])});
            skLineSegment(sketch, "E27.bottom", {"start": v(-41.85, 5.05) * mm, "end": v(-40.25, 5.05) * mm});
            skLineSegment(sketch, "E27.top", {"start": v(-41.85, -5.05) * mm, "end": v(-40.25, -5.05) * mm});
            skLineSegment(sketch, "E27.left", {"start": v(-41.85, 5.05) * mm, "end": v(-41.85, -5.05) * mm});
            skLineSegment(sketch, "E27.right", {"start": v(-40.25, 5.05) * mm, "end": v(-40.25, -5.05) * mm});
            skLineSegment(sketch, "E28", {"start": v(-41.85, 0) * mm, "end": v(-40.25, 0) * mm, "construction": true});
            skLineSegment(sketch, "E29", {"start": v(0, 8.73) * mm, "end": v(0, 0) * mm, "construction": true});
            skLineSegment(sketch, "E30.MirrorCS", {"start": v(40.25, 5.05) * mm, "end": v(40.25, -5.05) * mm});
            skLineSegment(sketch, "E31.MirrorCS", {"start": v(41.85, -5.05) * mm, "end": v(40.25, -5.05) * mm});
            skLineSegment(sketch, "E32.MirrorCS", {"start": v(41.85, 5.05) * mm, "end": v(41.85, -5.05) * mm});
            skLineSegment(sketch, "E33.MirrorCS", {"start": v(41.85, 5.05) * mm, "end": v(40.25, 5.05) * mm});
            skLineSegment(sketch, "E34.bottom", {"start": v(-5.05, -82.5) * mm, "end": v(5.05, -82.5) * mm});
            skLineSegment(sketch, "E34.top", {"start": v(-5.05, -80.9) * mm, "end": v(5.05, -80.9) * mm});
            skLineSegment(sketch, "E34.left", {"start": v(-5.05, -82.5) * mm, "end": v(-5.05, -80.9) * mm});
            skLineSegment(sketch, "E34.right", {"start": v(5.05, -82.5) * mm, "end": v(5.05, -80.9) * mm});
            skLineSegment(sketch, "E35", {"start": v(0, -80.9) * mm, "end": v(0, -82.5) * mm, "construction": true});
            skSolve(sketch);
        }
        {
            var Q0;
            Q0=qSketchRegion(id+"F41",true);
            extrude(context, id + "F42", {"entities" : qUnion([Q0]), "operationType" : NewBodyOperationType.REMOVE, "endBound" : BoundingType.UP_TO_NEXT, "oppositeDirection" : true, "depth" : 25 * mm});
        }
        {
            var Q0;
            Q0=qCreatedBy(id+"F19.planeOp",FACE);
            var sketch = newSketch(context, id + "F43", { "sketchPlane" : qUnion([Q0])});
            skLineSegment(sketch, "E36", {"start": v(56.35, -12) * mm, "end": v(56.35, 12) * mm});
            skLineSegment(sketch, "E37", {"start": v(56.35, 12) * mm, "end": v(53.35, 12) * mm});
            skLineSegment(sketch, "E38", {"start": v(53.35, 12) * mm, "end": v(53.35, 5) * mm});
            skLineSegment(sketch, "E39", {"start": v(53.35, 5) * mm, "end": v(54.85, 5) * mm});
            skLineSegment(sketch, "E40", {"start": v(54.85, 5) * mm, "end": v(54.85, -5) * mm});
            skLineSegment(sketch, "E41", {"start": v(54.85, -5) * mm, "end": v(53.35, -5) * mm});
            skLineSegment(sketch, "E42", {"start": v(53.35, -5) * mm, "end": v(53.35, -12) * mm});
            skLineSegment(sketch, "E43", {"start": v(53.35, -12) * mm, "end": v(56.35, -12) * mm});
            skLineSegment(sketch, "E44", {"start": v(54.85, 0) * mm, "end": v(40.9, 0) * mm, "construction": true});
            skLineSegment(sketch, "E45", {"start": v(0, 0) * mm, "end": v(0, -18) * mm, "construction": true});
            skLineSegment(sketch, "E46.MirrorCS", {"start": v(-56.35, -12) * mm, "end": v(-56.35, 12) * mm});
            skLineSegment(sketch, "E47.MirrorCS", {"start": v(-56.35, 12) * mm, "end": v(-53.35, 12) * mm});
            skLineSegment(sketch, "E48.MirrorCS", {"start": v(-53.35, 12) * mm, "end": v(-53.35, 5) * mm});
            skLineSegment(sketch, "E49.MirrorCS", {"start": v(-53.35, 5) * mm, "end": v(-54.85, 5) * mm});
            skLineSegment(sketch, "E50.MirrorCS", {"start": v(-54.85, 5) * mm, "end": v(-54.85, -5) * mm});
            skLineSegment(sketch, "E51.MirrorCS", {"start": v(-54.85, -5) * mm, "end": v(-53.35, -5) * mm});
            skLineSegment(sketch, "E52.MirrorCS", {"start": v(-53.35, -5) * mm, "end": v(-53.35, -12) * mm});
            skLineSegment(sketch, "E53.MirrorCS", {"start": v(-53.35, -12) * mm, "end": v(-56.35, -12) * mm});
            skLineSegment(sketch, "E54", {"start": v(12, -97) * mm, "end": v(-12, -97) * mm});
            skLineSegment(sketch, "E55", {"start": v(-12, -97) * mm, "end": v(-12, -94) * mm});
            skLineSegment(sketch, "E56", {"start": v(-12, -94) * mm, "end": v(-5, -94) * mm});
            skLineSegment(sketch, "E57", {"start": v(-5, -94) * mm, "end": v(-5, -95.5) * mm});
            skLineSegment(sketch, "E58", {"start": v(-5, -95.5) * mm, "end": v(5, -95.5) * mm});
            skLineSegment(sketch, "E59", {"start": v(5, -95.5) * mm, "end": v(5, -94) * mm});
            skLineSegment(sketch, "E60", {"start": v(5, -94) * mm, "end": v(12, -94) * mm});
            skLineSegment(sketch, "E61", {"start": v(12, -94) * mm, "end": v(12, -97) * mm});
            skLineSegment(sketch, "E62", {"start": v(0, -95.5) * mm, "end": v(0, -78.2) * mm, "construction": true});
            skSolve(sketch);
        }
        {
            var Q0;
            Q0=qSketchRegion(id+"F43",true);
            extrude(context, id + "F44", {"entities" : qUnion([Q0]), "operationType" : NewBodyOperationType.REMOVE, "endBound" : BoundingType.UP_TO_NEXT, "oppositeDirection" : true, "depth" : 25 * mm});
        }
        {
            var Q0;
            {var subQ2=sQuery(id+"F35.wireOp",EDGE,"E22.bottom");var subQ3=sQuery(id+"F23.wireOp",EDGE,"E11.right");Q0=makeQuery(id+"F44.boolean.opBoolean","SPLIT",FACE,{"disambiguationData":[TD([makeQuery(id+"F24.opExtrude","SWEPT_FACE",FACE,{"disambiguationData":[OSD([subQ3])]})])],"derivedFrom":makeQuery(id+"F36.boolean.opBoolean","MERGE",FACE,{"derivedFrom":[makeQuery(id+"F24.opExtrude","CAP_FACE",FACE,{"disambiguationData":[OSD([sQuery(id+"F23.wireOp",EDGE,"E11.bottom"),sQuery(id+"F23.wireOp",EDGE,"E11.top"),sQuery(id+"F23.wireOp",EDGE,"E11.left"),subQ3])],"isStart":false}),makeQuery(id+"F36.opExtrude","SWEPT_FACE",FACE,{"disambiguationData":[OSD([subQ2])]}),makeQuery(id+"F36.opExtrude","SWEPT_FACE",FACE,{"disambiguationData":[OSD([sQuery(id+"F35.wireOp",EDGE,"E23.bottom")])]})]})});}
            var sketch = newSketch(context, id + "F45", { "sketchPlane" : qUnion([Q0])});
            skLineSegment(sketch, "E63.bottom", {"start": v(-6, 22.5) * mm, "end": v(6, 22.5) * mm});
            skLineSegment(sketch, "E63.top", {"start": v(-6, 20) * mm, "end": v(6, 20) * mm});
            skLineSegment(sketch, "E63.left", {"start": v(-6, 22.5) * mm, "end": v(-6, 20) * mm});
            skLineSegment(sketch, "E63.right", {"start": v(6, 22.5) * mm, "end": v(6, 20) * mm});
            skSolve(sketch);
        }
        {
            var Q0;
            Q0=qSketchRegion(id+"F45",true);
            extrude(context, id + "F46", {"entities" : qUnion([Q0]), "operationType" : NewBodyOperationType.ADD, "oppositeDirection" : true, "depth" : 3 * mm});
        }
        {
            var Q0;
            Q0=makeQuery(id+"F15.opExtrude","SWEPT_BODY",BODY,{"disambiguationData":[OSD([sQuery(id+"F14.wireOp",EDGE,"E9.bottom"),sQuery(id+"F14.wireOp",EDGE,"E9.top"),sQuery(id+"F14.wireOp",EDGE,"E9.left"),sQuery(id+"F14.wireOp",EDGE,"E9.right")])]});
            deleteBodies(context, id + "F47", {"entities" : qUnion([Q0])});
        }
    });
